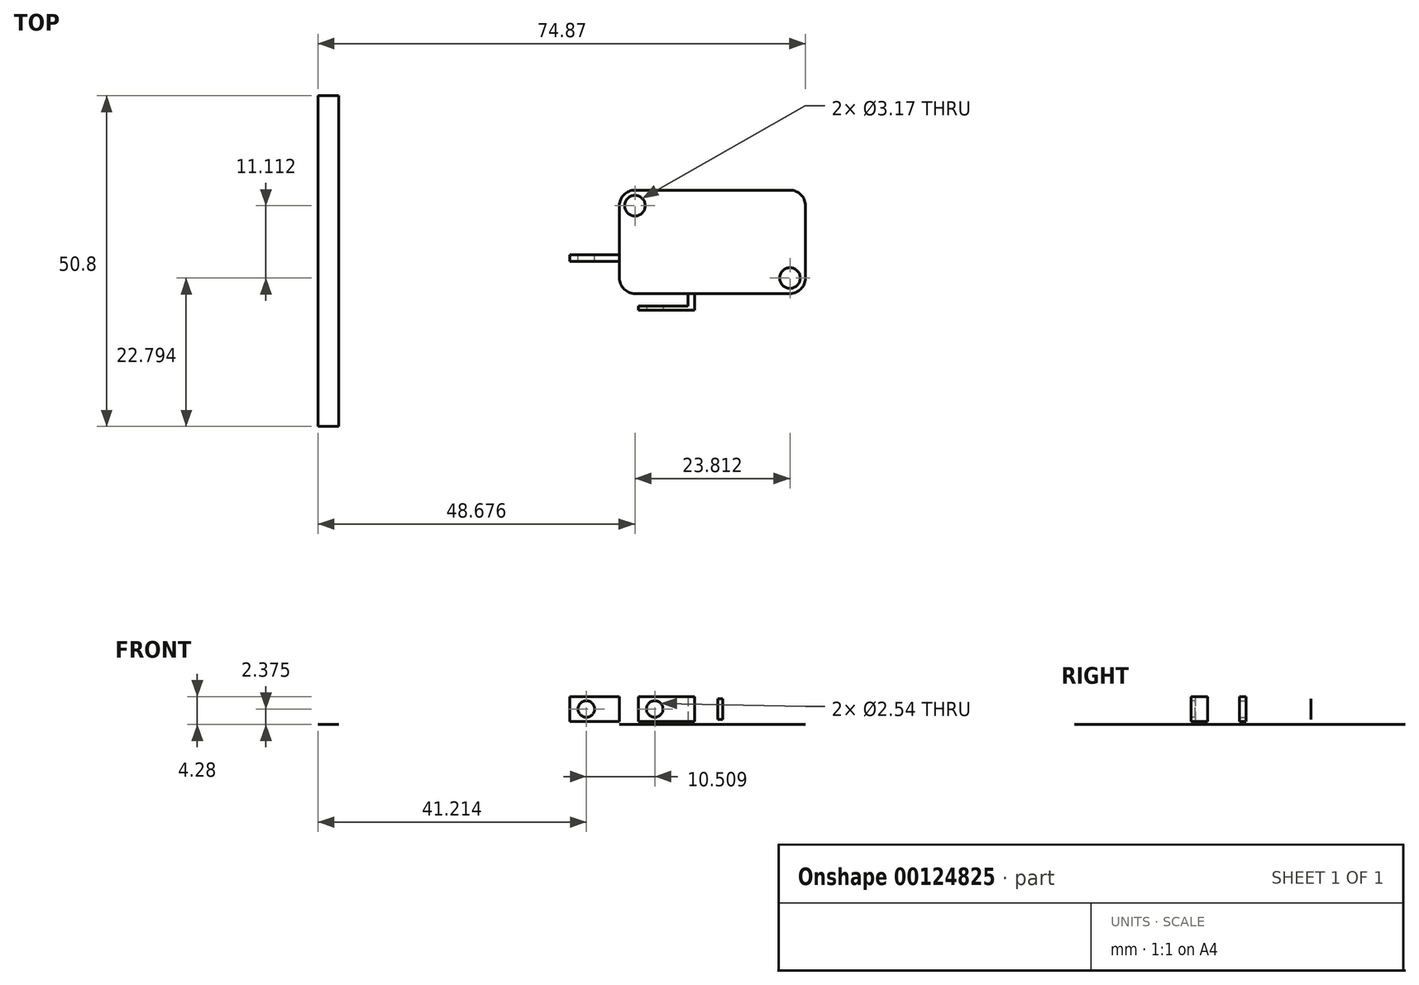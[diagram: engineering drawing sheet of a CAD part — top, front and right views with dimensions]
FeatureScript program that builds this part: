
annotation { "Feature Type Name" : "Feature", "Feature Type Description" : "" }
export const myFeature = defineFeature(function(context is Context, id is Id, definition is map)
    precondition{}
    {
        {
            var Q0;
            Q0=qCreatedBy(makeId("Top.planeOp"),FACE);
            var sketch = newSketch(context, id + "F0", { "sketchPlane" : qUnion([Q0])});
            skLineSegment(sketch, "E0.bottom", {"start": v(-21.25, 22.68) * mm, "end": v(7.33, 22.68) * mm});
            skLineSegment(sketch, "E0.top", {"start": v(-21.25, 6.8) * mm, "end": v(7.33, 6.8) * mm});
            skLineSegment(sketch, "E0.left", {"start": v(-21.25, 22.68) * mm, "end": v(-21.25, 6.8) * mm});
            skLineSegment(sketch, "E0.right", {"start": v(7.33, 22.68) * mm, "end": v(7.33, 6.8) * mm});
            skCircle(sketch, "E1", {"center": v(-18.86, 20.3) * mm, "radius": 2.38 * mm});
            skCircle(sketch, "E2", {"center": v(4.95, 9.18) * mm, "radius": 2.38 * mm});
            skCircle(sketch, "E3", {"center": v(4.95, 20.3) * mm, "radius": 2.38 * mm});
            skCircle(sketch, "E4", {"center": v(-18.86, 9.18) * mm, "radius": 2.38 * mm});
            skCircle(sketch, "E5", {"center": v(-18.86, 20.3) * mm, "radius": 1.59 * mm});
            skCircle(sketch, "E6", {"center": v(4.95, 9.18) * mm, "radius": 1.59 * mm});
            skSolve(sketch);
        }
        {
            var Q0;
            {var subQ0=sQuery(id+"F0.wireOp",EDGE,"E3");var subQ1=makeQuery(id+"F0.imprint","INTERSECT",VERTEX,{"derivedFrom":[sQuery(id+"F0.wireOp",EDGE,"E0.bottom"),subQ0]});Q0=makeQuery(id+"F0.imprint","IMPRINT",FACE,{"disambiguationData":[TD([[makeQuery(id+"F0.imprint","IMPRINT",EDGE,{"disambiguationData":[TD([[subQ1,1.0]])],"derivedFrom":subQ0}),1.0]])]});}
            var Q1;
            {var subQ0=sQuery(id+"F0.wireOp",EDGE,"E4");var subQ1=makeQuery(id+"F0.imprint","INTERSECT",VERTEX,{"derivedFrom":[sQuery(id+"F0.wireOp",EDGE,"E0.top"),subQ0]});Q1=makeQuery(id+"F0.imprint","IMPRINT",FACE,{"disambiguationData":[TD([[makeQuery(id+"F0.imprint","IMPRINT",EDGE,{"disambiguationData":[TD([[subQ1,1.0]])],"derivedFrom":subQ0}),1.0]])]});}
            var Q2;
            Q2=makeQuery(id+"F0.imprint","IMPRINT",FACE,{"disambiguationData":[TD([[makeQuery(id+"F0.imprint","IMPRINT",EDGE,{"derivedFrom":sQuery(id+"F0.wireOp",EDGE,"E5")}),-1.0]])]});
            var Q3;
            Q3=makeQuery(id+"F0.imprint","IMPRINT",FACE,{"disambiguationData":[TD([[makeQuery(id+"F0.imprint","IMPRINT",EDGE,{"derivedFrom":sQuery(id+"F0.wireOp",EDGE,"E6")}),-1.0]])]});
            var Q4;
            {var subQ5=sQuery(id+"F0.wireOp",EDGE,"E1");var subQ13=sQuery(id+"F0.wireOp",EDGE,"E0.bottom");var subQ14=makeQuery(id+"F0.imprint","INTERSECT",VERTEX,{"derivedFrom":[subQ13,subQ5]});Q4=makeQuery(id+"F0.imprint","IMPRINT",FACE,{"disambiguationData":[TD([[makeQuery(id+"F0.imprint","IMPRINT",EDGE,{"disambiguationData":[TD([[subQ14,-1.0]])],"derivedFrom":subQ13}),-1.0]])]});}
            extrude(context, id + "F1", {"entities" : qUnion([Q0, Q1, Q2, Q3, Q4]), "depth" : 3 / 406.4 * mm});
        }
        {
            var Q0;
            Q0=qCreatedBy(makeId("Top.planeOp"),FACE);
            var sketch = newSketch(context, id + "F2", { "sketchPlane" : qUnion([Q0])});
            skLineSegment(sketch, "E7.bottom", {"start": v(-67.54, 37.19) * mm, "end": v(-64.36, 37.19) * mm});
            skLineSegment(sketch, "E7.top", {"start": v(-67.54, -13.61) * mm, "end": v(-64.36, -13.61) * mm});
            skLineSegment(sketch, "E7.left", {"start": v(-67.54, 37.19) * mm, "end": v(-67.54, -13.61) * mm});
            skLineSegment(sketch, "E7.right", {"start": v(-64.36, 37.19) * mm, "end": v(-64.36, -13.61) * mm});
            skSolve(sketch);
        }
        {
            var Q0;
            Q0=qSketchRegion(id+"F2",true);
            extrude(context, id + "F3", {"entities" : qUnion([Q0]), "depth" : 1 / 812.8 * mm});
        }
        {
            var Q0;
            Q0=makeQuery(id+"F1.opExtrude","SWEPT_FACE",FACE,{"disambiguationData":[OSD([sQuery(id+"F0.wireOp",EDGE,"E0.bottom")])]});
            var sketch = newSketch(context, id + "F4", { "sketchPlane" : qUnion([Q0])});
            skLineSegment(sketch, "E8.bottom", {"start": v(6.16, 0.76) * mm, "end": v(5.37, 0.76) * mm});
            skLineSegment(sketch, "E8.top", {"start": v(6.16, 3.94) * mm, "end": v(5.37, 3.94) * mm});
            skLineSegment(sketch, "E8.left", {"start": v(6.16, 0.76) * mm, "end": v(6.16, 3.94) * mm});
            skLineSegment(sketch, "E8.right", {"start": v(5.37, 0.76) * mm, "end": v(5.37, 3.94) * mm});
            skSolve(sketch);
        }
        {
            var Q0;
            Q0=qSketchRegion(id+"F4",true);
            extrude(context, id + "F5", {"entities" : qUnion([Q0]), "operationType" : NewBodyOperationType.ADD, "depth" : 1 / 812.8 * mm});
        }
        {
            var Q0;
            Q0=makeQuery(id+"F1.opExtrude","SWEPT_FACE",FACE,{"disambiguationData":[OSD([sQuery(id+"F0.wireOp",EDGE,"E0.top")])]});
            var sketch = newSketch(context, id + "F6", { "sketchPlane" : qUnion([Q0])});
            skLineSegment(sketch, "E9.bottom", {"start": v(-10.74, 4.28) * mm, "end": v(-9.72, 4.28) * mm});
            skLineSegment(sketch, "E9.top", {"start": v(-10.74, 0.47) * mm, "end": v(-9.72, 0.47) * mm});
            skLineSegment(sketch, "E9.left", {"start": v(-10.74, 4.28) * mm, "end": v(-10.74, 0.47) * mm});
            skLineSegment(sketch, "E9.right", {"start": v(-9.72, 4.28) * mm, "end": v(-9.72, 0.47) * mm});
            skSolve(sketch);
        }
        {
            var Q0;
            Q0=qSketchRegion(id+"F6",true);
            extrude(context, id + "F7", {"entities" : qUnion([Q0]), "operationType" : NewBodyOperationType.ADD, "depth" : 2.54 * mm});
        }
        {
            var Q0;
            Q0=makeQuery(id+"F7.opExtrude","SWEPT_FACE",FACE,{"disambiguationData":[OSD([sQuery(id+"F6.wireOp",EDGE,"E9.left")])]});
            var sketch = newSketch(context, id + "F8", { "sketchPlane" : qUnion([Q0])});
            skLineSegment(sketch, "E10.bottom", {"start": v(-4.26, 4.28) * mm, "end": v(-4.9, 4.28) * mm});
            skLineSegment(sketch, "E10.top", {"start": v(-4.26, 0.47) * mm, "end": v(-4.9, 0.47) * mm});
            skLineSegment(sketch, "E10.left", {"start": v(-4.26, 4.28) * mm, "end": v(-4.26, 0.47) * mm});
            skLineSegment(sketch, "E10.right", {"start": v(-4.9, 4.28) * mm, "end": v(-4.9, 0.47) * mm});
            skSolve(sketch);
        }
        {
            var Q0;
            Q0=qSketchRegion(id+"F8",true);
            extrude(context, id + "F9", {"entities" : qUnion([Q0]), "operationType" : NewBodyOperationType.ADD, "depth" : 7.62 * mm});
        }
        {
            var Q0;
            Q0=makeQuery(id+"F9.boolean.opBoolean","MERGE",FACE,{"derivedFrom":[makeQuery(id+"F7.opExtrude","CAP_FACE",FACE,{"disambiguationData":[OSD([sQuery(id+"F6.wireOp",EDGE,"E9.bottom"),sQuery(id+"F6.wireOp",EDGE,"E9.top"),sQuery(id+"F6.wireOp",EDGE,"E9.left"),sQuery(id+"F6.wireOp",EDGE,"E9.right")])],"isStart":false}),makeQuery(id+"F9.opExtrude","SWEPT_FACE",FACE,{"disambiguationData":[OSD([sQuery(id+"F8.wireOp",EDGE,"E10.left")])]})]});
            var sketch = newSketch(context, id + "F10", { "sketchPlane" : qUnion([Q0])});
            skCircle(sketch, "E11", {"center": v(-15.82, 2.37) * mm, "radius": 1.27 * mm});
            skSolve(sketch);
        }
        {
            var Q0;
            Q0=qSketchRegion(id+"F10",true);
            extrude(context, id + "F11", {"entities" : qUnion([Q0]), "operationType" : NewBodyOperationType.REMOVE, "oppositeDirection" : true, "depth" : 1.17 * mm});
        }
        {
            var Q0;
            Q0=makeQuery(id+"F1.opExtrude","SWEPT_FACE",FACE,{"disambiguationData":[OSD([sQuery(id+"F0.wireOp",EDGE,"E0.left")])]});
            var sketch = newSketch(context, id + "F12", { "sketchPlane" : qUnion([Q0])});
            skLineSegment(sketch, "E12.bottom", {"start": v(-12.74, 4.28) * mm, "end": v(-11.72, 4.28) * mm});
            skLineSegment(sketch, "E12.top", {"start": v(-12.74, 0.47) * mm, "end": v(-11.72, 0.47) * mm});
            skLineSegment(sketch, "E12.left", {"start": v(-12.74, 4.28) * mm, "end": v(-12.74, 0.47) * mm});
            skLineSegment(sketch, "E12.right", {"start": v(-11.72, 4.28) * mm, "end": v(-11.72, 0.47) * mm});
            skSolve(sketch);
        }
        {
            var Q0;
            Q0=qSketchRegion(id+"F12",true);
            extrude(context, id + "F13", {"entities" : qUnion([Q0]), "operationType" : NewBodyOperationType.ADD, "depth" : 7.62 * mm});
        }
        {
            var Q0;
            Q0=makeQuery(id+"F13.opExtrude","SWEPT_FACE",FACE,{"disambiguationData":[OSD([sQuery(id+"F12.wireOp",EDGE,"E12.left")])]});
            var sketch = newSketch(context, id + "F14", { "sketchPlane" : qUnion([Q0])});
            skCircle(sketch, "E13", {"center": v(26.33, 2.37) * mm, "radius": 1.27 * mm});
            skSolve(sketch);
        }
        {
            var Q0;
            Q0=makeQuery(id+"F14.imprint","IMPRINT",FACE,{"disambiguationData":[TD([[makeQuery(id+"F14.imprint","IMPRINT",EDGE,{"derivedFrom":sQuery(id+"F14.wireOp",EDGE,"E13")}),1.0]])]});
            extrude(context, id + "F15", {"entities" : qUnion([Q0]), "operationType" : NewBodyOperationType.REMOVE, "oppositeDirection" : true, "depth" : 25.4 * mm});
        }
    });
